# Revit family: Холодильные шкафы для вина
name_source: partatom
category: Оборудование
units: mm (PartAtom-declared; Revit-internal decimal feet)

## family parameters
Всегда вертикально = Да
Классификация = Нет
На основе рабочей плоскости = Нет
Общий = Нет
При загрузке вырезать с полостями = Нет
Размер круглого соединителя = Использовать диаметр
Тип детали = Нормальный
Точка расчета площади = Нет

## types (1)
- DW102-Bravo
    Вес брутто, кг = 65
    Вес нетто, кг = 58
    Высота = 890 мм
    Габаритные размеры, мм = 606х625х890
    Глубина = 625 мм
    Диап. рабочих температур = +4....+18
    Допустимая нагрузка на полку, кг = 40
    Замок = +
    Кол-во полок = 2
    Объем, л. = 150
    Отметка по умолчанию = 0 мм
    Подсветка = LED
    Размеры в упаковке, мм = 720х660х1100
    Система обновления воздуха = +
    Система электропитания В/Гц = 230/50
    Терморегулятор = эл.  блок
    Тип оттайки = автом. с системой испарения конденсата
    Тип охлаждения = статический
    Тонированое стекло с УФ-защитой = +
    Угольный фильтр = +
    Условия окр. среды (темп./вл-сть,%) = до +32/до 60
    Хладагент = R134a
    Холодильный шкаф = <По категории>
    Цена, руб. = 38 380
    Ширина = 606 мм
